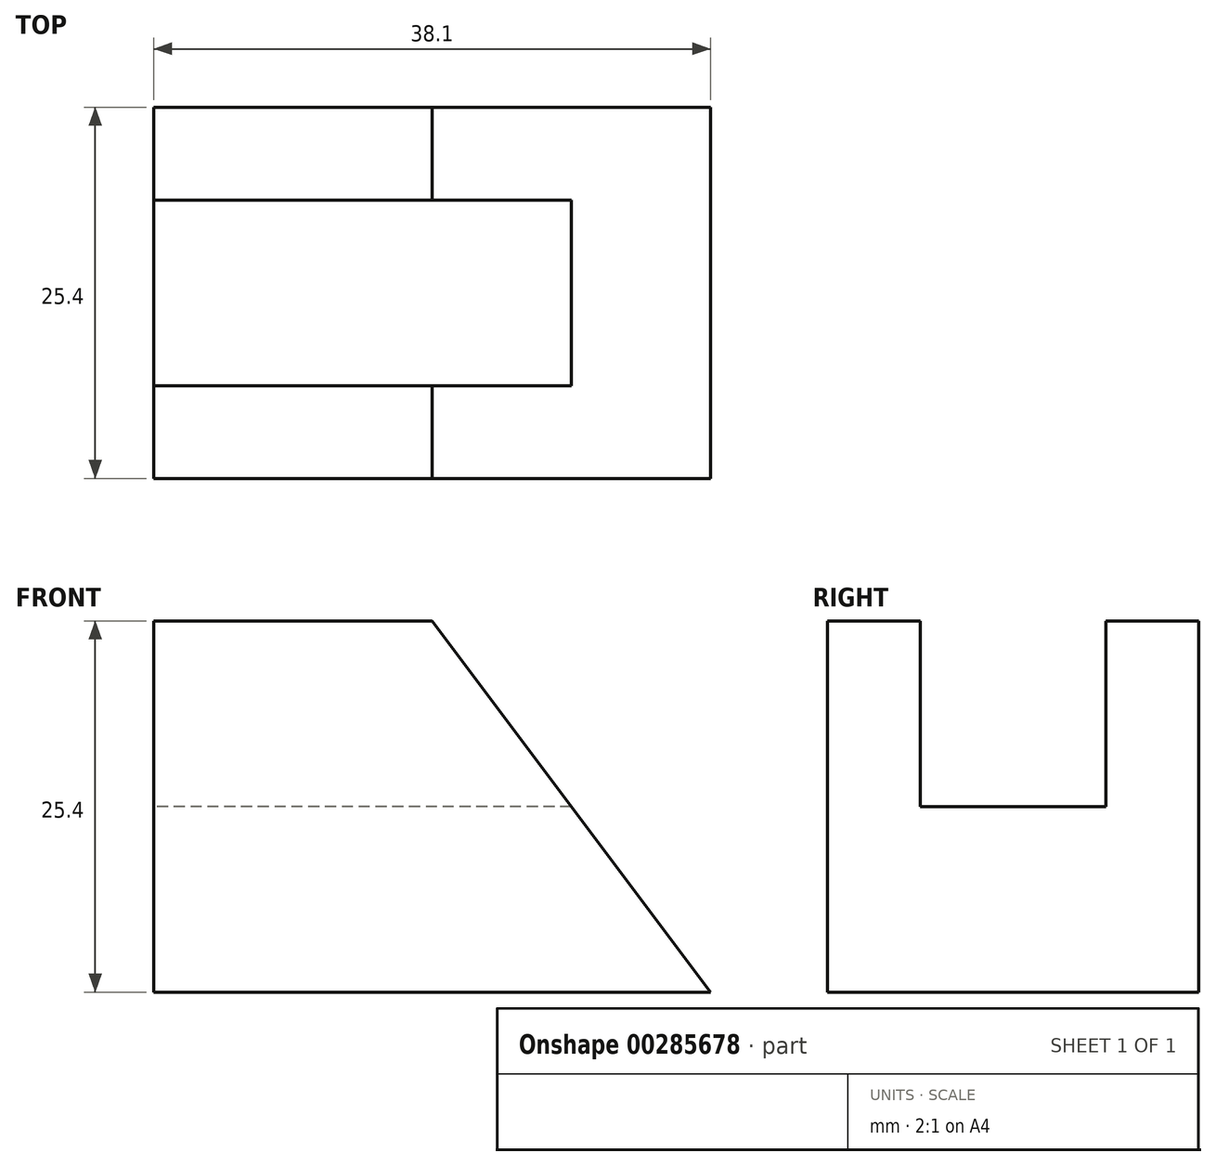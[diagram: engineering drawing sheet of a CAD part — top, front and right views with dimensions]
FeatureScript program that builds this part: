
annotation { "Feature Type Name" : "Feature", "Feature Type Description" : "" }
export const myFeature = defineFeature(function(context is Context, id is Id, definition is map)
    precondition{}
    {
        {
            var Q0;
            Q0=qCreatedBy(makeId("Front.planeOp"),FACE);
            var sketch = newSketch(context, id + "F0", { "sketchPlane" : qUnion([Q0])});
            skLineSegment(sketch, "E0", {"start": v(0, 0) * mm, "end": v(0, 25.4) * mm});
            skLineSegment(sketch, "E1", {"start": v(0, 25.4) * mm, "end": v(19.05, 25.4) * mm});
            skLineSegment(sketch, "E2", {"start": v(19.05, 25.4) * mm, "end": v(38.1, 0) * mm});
            skLineSegment(sketch, "E3", {"start": v(38.1, 0) * mm, "end": v(0, 0) * mm});
            skSolve(sketch);
        }
        {
            var Q0;
            Q0=makeQuery(id+"F0.imprint","IMPRINT",FACE,{"disambiguationData":[TD([[makeQuery(id+"F0.imprint","IMPRINT",EDGE,{"derivedFrom":sQuery(id+"F0.wireOp",EDGE,"E0")}),-1.0]])]});
            extrude(context, id + "F1", {"entities" : qUnion([Q0]), "depth" : 25.4 * mm});
        }
        {
            var Q0;
            Q0=makeQuery(id+"F1.opExtrude","SWEPT_FACE",FACE,{"disambiguationData":[OSD([sQuery(id+"F0.wireOp",EDGE,"E0")])]});
            var sketch = newSketch(context, id + "F2", { "sketchPlane" : qUnion([Q0])});
            skLineSegment(sketch, "E4.bottom", {"start": v(6.35, 25.4) * mm, "end": v(19.05, 25.4) * mm});
            skLineSegment(sketch, "E4.top", {"start": v(6.35, 12.7) * mm, "end": v(19.05, 12.7) * mm});
            skLineSegment(sketch, "E4.left", {"start": v(6.35, 25.4) * mm, "end": v(6.35, 12.7) * mm});
            skLineSegment(sketch, "E4.right", {"start": v(19.05, 25.4) * mm, "end": v(19.05, 12.7) * mm});
            skSolve(sketch);
        }
        {
            var Q0;
            Q0=makeQuery(id+"F2.imprint","IMPRINT",FACE,{"disambiguationData":[TD([[makeQuery(id+"F2.imprint","IMPRINT",EDGE,{"derivedFrom":sQuery(id+"F2.wireOp",EDGE,"E4.bottom")}),1.0]])]});
            extrude(context, id + "F3", {"entities" : qUnion([Q0]), "operationType" : NewBodyOperationType.REMOVE, "endBound" : BoundingType.THROUGH_ALL, "oppositeDirection" : true, "depth" : 25.4 * mm});
        }
    });
